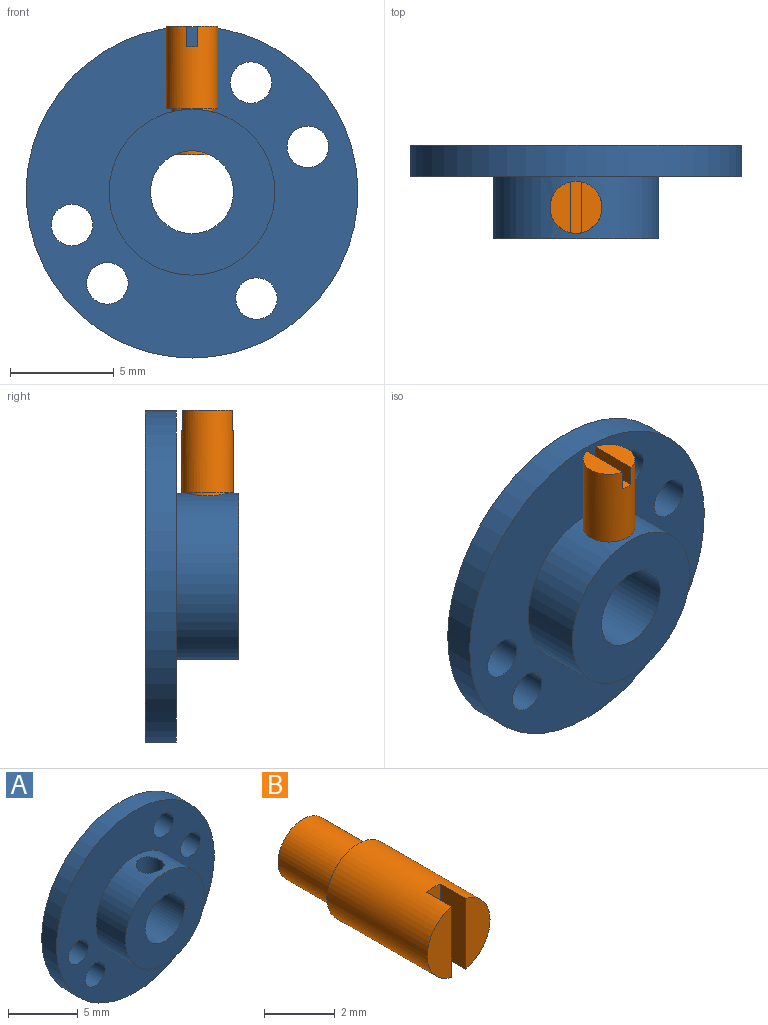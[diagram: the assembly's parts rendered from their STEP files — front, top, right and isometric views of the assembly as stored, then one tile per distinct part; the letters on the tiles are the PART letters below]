
ASSEMBLY  parts=2 mates=1
PART A: 12 faces, bbox 16x4.5x16 mm
  f0: cylinder r=2mm len=4.5mm, axis (0,1,0), area 53.3mm2, adj f4,f5,f11
  f1: cylinder r=4mm len=8mm, axis (0,1,0), area 72.2mm2, adj f3,f5,f11
  f2: cylinder r=8mm len=16mm, axis (0,1,0), area 75.4mm2, adj f3,f4
  f3: plane 16x16mm, normal (0,-1,0), area 135.1mm2, adj f1,f2,f6,f7,f8,f9,f10
  f4: plane 16x16mm, normal (0,1,0), area 172.8mm2, adj f0,f2,f6,f7,f8,f9,f10
  f5: plane 8x8mm, normal (0,-1,0), area 37.7mm2, adj f0,f1
  f6: cylinder r=1mm len=2mm, axis (0,-1,0), area 9.4mm2, adj f3,f4
  f7: cylinder r=1mm len=2mm, axis (0,-1,0), area 9.4mm2, adj f3,f4
  f8: cylinder r=1mm len=2mm, axis (0,-1,0), area 9.4mm2, adj f3,f4
  f9: cylinder r=1mm len=2mm, axis (0,-1,0), area 9.4mm2, adj f3,f4
  f10: cylinder r=1mm len=2mm, axis (0,-1,0), area 9.4mm2, adj f3,f4
  f11: cylinder r=1mm len=2.27mm, axis (0,0,-1), area 13mm2, adj f0,f1
PART B: 9 faces, bbox 2.5x6.2x2.5 mm
  f0: cylinder r=1.25mm len=4mm, axis (0,1,0), area 30.3mm2, adj f1,f4,f5,f6,f7,f8
  f1: plane 2.44x0.97mm, normal (0,-1,0), area 1.8mm2, adj f0,f7
  f2: cylinder r=1mm len=2.2mm, axis (0,1,0), area 13.8mm2, adj f3,f5
  f3: plane 2x2mm, normal (0,1,0), area 3.1mm2, adj f2
  f4: plane 2.44x0.97mm, normal (0,-1,0), area 1.8mm2, adj f0,f8
  f5: plane 2.5x2.5mm, normal (0,1,0), area 1.8mm2, adj f0,f2
  f6: plane 2.5x0.55mm, normal (0,-1,0), area 1.4mm2, adj f0,f7,f8
  f7: plane 2.44x1mm, normal (-1,0,0), area 2.4mm2, adj f0,f1,f6
  f8: plane 2.44x1mm, normal (1,0,0), area 2.4mm2, adj f0,f4,f6
PLACE A t=(-3.92,0.35,-0.46)mm
PLACE B rot(axis=(-1,0,0),90deg) t=(-3.92,-2.65,1.36)mm
MATE fastened B.f2 <-> A.f11  axis (0,0,-1) through (-3.92,-2.65,3.56)mm
